# Revit family: PLL - DELIVERY 1 VARIATIONS - PARTS
name_source: partatom
category: Generic Models
revit_build: Autodesk Revit 2017 (Build: 20160225_1515(x64)
units: mm (PartAtom-declared; Revit-internal decimal feet)

## family parameters
Always vertical = Yes
Can host rebar = No
Cut with Voids When Loaded = No
Part Type = Normal
Room Calculation Point = No
Round Connector Dimension = Use Diameter
Shared = No
Work Plane-Based = No

## types (5) — shared parameters

## per-type parameters (varying)
| type | C_alteza da terra | larghezza | profondità |
| 30x60cm | 1300 mm  [stored 4.26509 ft] | 300 mm | 500 mm  [stored 1.64042 ft] |
| 50x60cm | 500 mm  [stored 1.64042 ft] | 500 mm  [stored 1.64042 ft] | 500 mm  [stored 1.64042 ft] |
| 60x60cm | 3000 mm  [stored 9.84252 ft] | 600 mm | 600 mm |
| 20x60cm | 100 mm  [stored 0.328084 ft] | 300 mm | 500 mm  [stored 1.64042 ft] |
| 10x60cm | 1000 mm  [stored 3.28084 ft] | 300 mm | 500 mm  [stored 1.64042 ft] |

note: [stored X ft] marks values corroborated as IEEE doubles in the binary element streams (Revit-internal decimal feet)

## geometry (parser evidence)
native form markers: Sweep x3
no freeform markers — native parametric forms only
